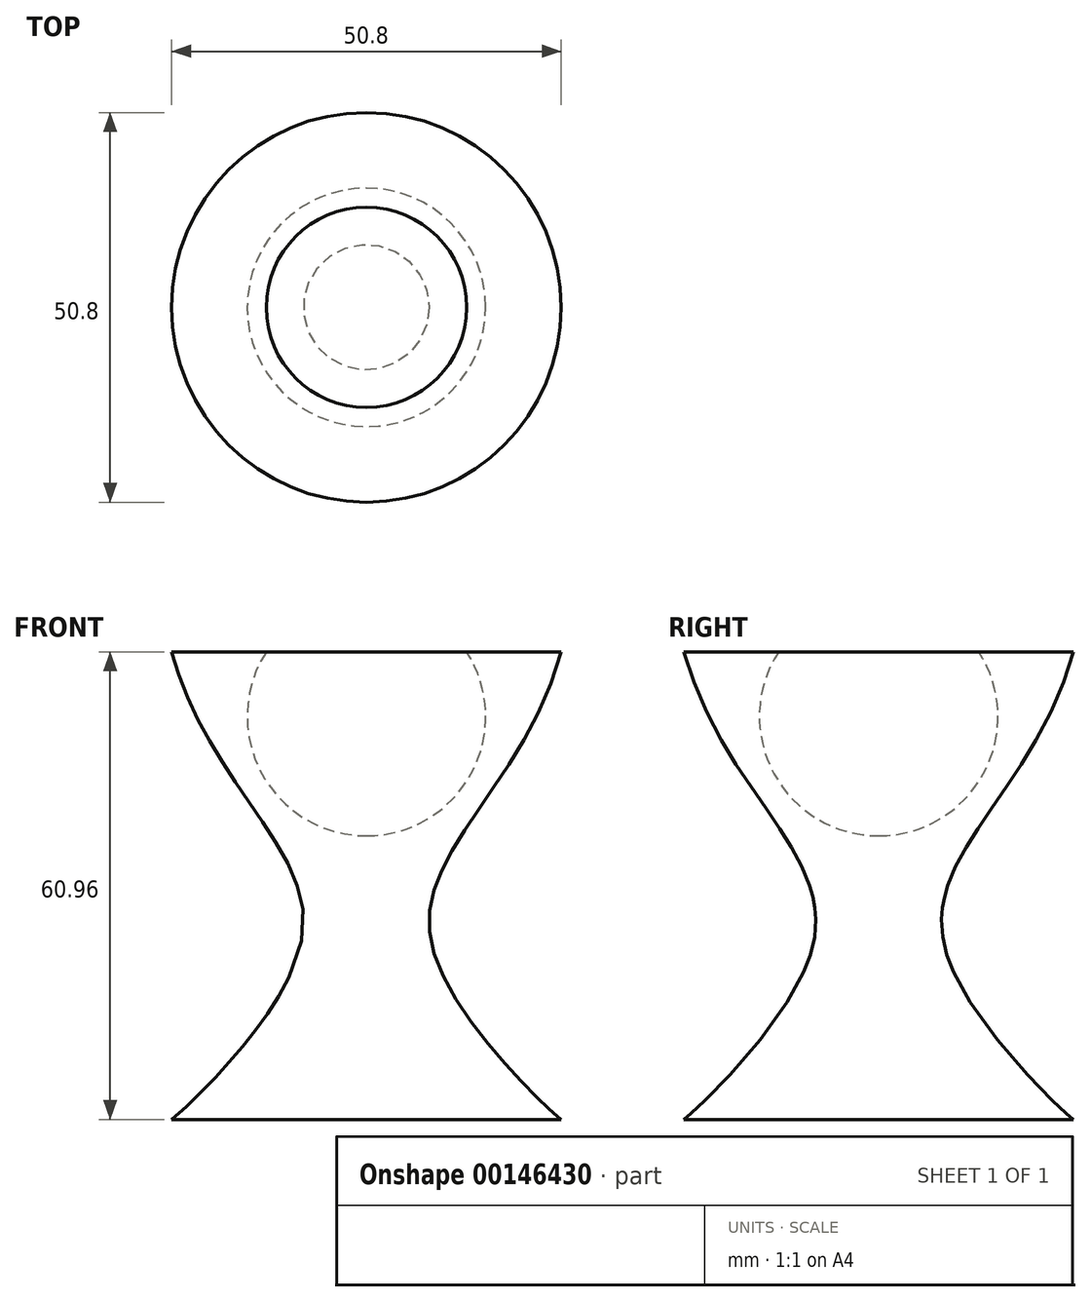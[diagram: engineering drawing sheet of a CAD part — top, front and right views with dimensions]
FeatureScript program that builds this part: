
annotation { "Feature Type Name" : "Feature", "Feature Type Description" : "" }
export const myFeature = defineFeature(function(context is Context, id is Id, definition is map)
    precondition{}
    {
        {
            var Q0;
            Q0=qCreatedBy(makeId("Top.planeOp"),FACE);
            var sketch = newSketch(context, id + "F0", { "sketchPlane" : qUnion([Q0])});
            skCircle(sketch, "E0", {"center": v(0, 0) * mm, "radius": 25.4 * mm});
            skSolve(sketch);
        }
        {
            var Q0;
            Q0 = qSketchRegion(id + "F0", true);
            extrude(context, id + "F1", {"entities" : qUnion([Q0]), "depth" : 60.96 * mm});
        }
        {
            var Q0;
            Q0=qCreatedBy(makeId("Front.planeOp"),FACE);
            var sketch = newSketch(context, id + "F2", { "sketchPlane" : qUnion([Q0])});
            skLineSegment(sketch, "E1", {"start": v(-25.4, 64.45) * mm, "end": v(-25.4, 23.6) * mm, "construction": true});
            skLineSegment(sketch, "E2", {"start": v(0, 63.73) * mm, "end": v(0, 23.6) * mm, "construction": true});
            skLineSegment(sketch, "E3", {"start": v(-25.4, 60.96) * mm, "end": v(41.38, 60.96) * mm, "construction": true});
            skFitSpline(sketch, "E4", {"points": [v(-25.4, 60.96) * mm, v(-8.53, 22.79) * mm, v(-25.4, 0) * mm], "startDerivative": vector(27.43, -99.5) * mm, "endDerivative": vector(-3.25, -1.32) * mm});
            skLineSegment(sketch, "E5", {"start": v(-25.4, 60.96) * mm, "end": v(-25.4, 0) * mm});
            skSolve(sketch);
        }
        {
            var Q0;
            Q0 = qSketchRegion(id + "F2", true);
            var Q1;
            Q1=sQuery(id+"F2.wireOp",EDGE,"E2");
            revolve(context, id + "F3", {"operationType" : NewBodyOperationType.REMOVE, "entities" : qUnion([Q0]), "axis" : qUnion([Q1]), "revolveType" : RevolveType.FULL});
        }
        {
            var Q0;
            Q0=qCreatedBy(makeId("Front.planeOp"),FACE);
            var sketch = newSketch(context, id + "F4", { "sketchPlane" : qUnion([Q0])});
            skArc(sketch, "E6", {"start": v(0, 36.97) * mm, "mid": v(15.55, 52.52) * mm, "end": v(0, 68.07) * mm});
            skLineSegment(sketch, "E7", {"start": v(0, 70.86) * mm, "end": v(0, 65.28) * mm});
            skLineSegment(sketch, "E8", {"start": v(0, 65.28) * mm, "end": v(0, 36.97) * mm});
            skSolve(sketch);
        }
        {
            var Q0;
            Q0 = qSketchRegion(id + "F4", true);
            var Q1;
            Q1=sQuery(id+"F4.wireOp",EDGE,"E8");
            revolve(context, id + "F5", {"operationType" : NewBodyOperationType.REMOVE, "entities" : qUnion([Q0]), "axis" : qUnion([Q1]), "revolveType" : RevolveType.FULL, "oppositeDirection" : true});
        }
    });
